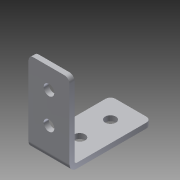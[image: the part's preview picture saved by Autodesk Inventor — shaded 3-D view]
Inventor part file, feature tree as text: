
AUTODESK INVENTOR PART (.ipt)
format: ipt  version: 2013 (Build 170138000, 138)  size: 184,832 bytes
history: native  units: in
note: dims shown in document units (in); Inventor stores cm internally (conversion verified against a paired STEP export)
features: sheet_metal_op x4, other x4, sketch x3, chamfer x1
ambient origin geometry x8: Origin, YZ Plane, XZ Plane, XY Plane, X Axis, Y Axis, Z Axis, Center Point
bodies: Solid1 (feature_tree)
feature tree (12):
  sheet_metal_op  "Face1"
  sheet_metal_op  "Flange1"
  chamfer  "Corner Round1"
  sketch  "Sketch1"  dims[d0=0.26in]
  other  "Plate1"
  sketch  "Sketch2"  dims[d2=1.0in]
  other  "Plate2"
  sheet_metal_op  "Bend1"
  sheet_metal_op  "Corner1"
  sketch  "Sketch3"  dims[d3=2.0in d4=0.75in d5=0.75in d6=0.125in d7=0.125in d8=0.0625in d9=0.25in d10=0.125in d11=2.0in d12=90.0deg d13=0.05in d14=0.5in d15=0.125in d16=0.125in d17=0.75in d18=0.75in d19=0.26in d20=0.125in d21=0.0in d22=0.125in]
  other  "Cut1"
  other  "Definition1"
